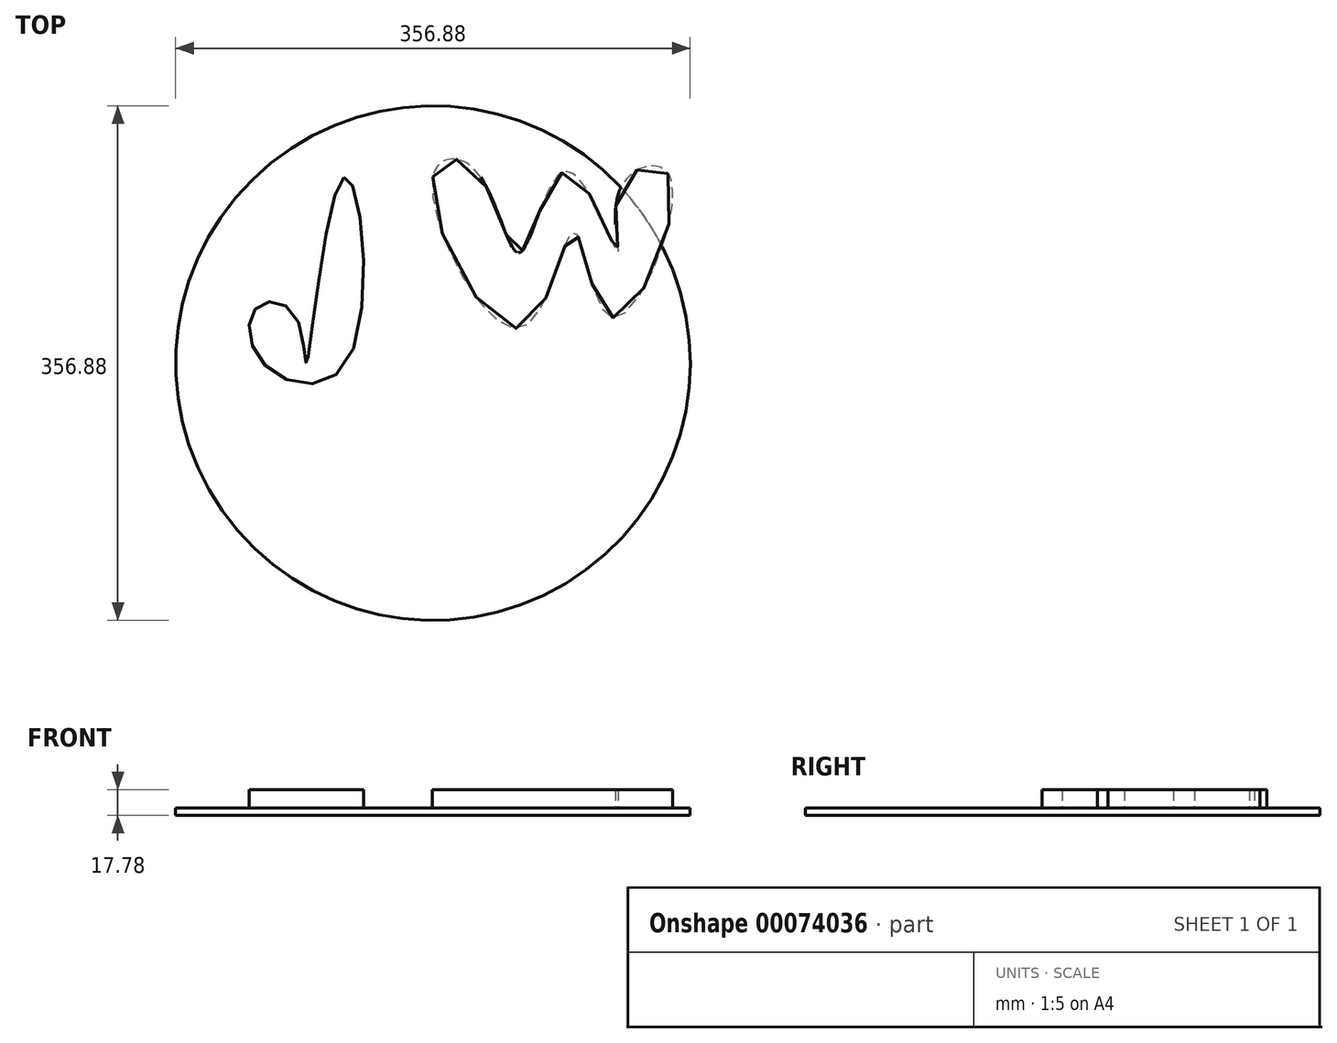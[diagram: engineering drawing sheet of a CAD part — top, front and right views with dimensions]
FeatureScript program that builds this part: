
annotation { "Feature Type Name" : "Feature", "Feature Type Description" : "" }
export const myFeature = defineFeature(function(context is Context, id is Id, definition is map)
    precondition{}
    {
        {
            var Q0;
            Q0=qCreatedBy(makeId("Top.planeOp"),FACE);
            var sketch = newSketch(context, id + "F0", { "sketchPlane" : qUnion([Q0])});
            skCircle(sketch, "E0", {"center": v(0, 0) * mm, "radius": 178.44 * mm});
            skSolve(sketch);
        }
        {
            var Q0;
            Q0=makeQuery(id+"F0.imprint","IMPRINT",FACE,{"disambiguationData":[TD([[makeQuery(id+"F0.imprint","IMPRINT",EDGE,{"derivedFrom":sQuery(id+"F0.wireOp",EDGE,"E0")}),1.0]])]});
            extrude(context, id + "F2", {"entities" : qUnion([Q0]), "depth" : 5.08 * mm});
        }
        {
            var Q0;
            Q0=makeQuery(id+"F2.opExtrude","CAP_FACE",FACE,{"disambiguationData":[OSD([sQuery(id+"F0.wireOp",EDGE,"E0")])],"isStart":false});
            var sketch = newSketch(context, id + "F3", { "sketchPlane" : qUnion([Q0])});
            skFitSpline(sketch, "E1", {"points": [v(-61.85, 129.01) * mm, v(-60.08, 0) * mm, v(-117.84, 0) * mm, v(-122.23, 38.62) * mm, v(-95.67, 33.35) * mm, v(-87.68, 0) * mm, v(-61.85, 129.01) * mm]});
            skFitSpline(sketch, "E2", {"points": [v(0, 129.21) * mm, v(61.34, 24.47) * mm, v(97.81, 91.15) * mm, v(124.24, 31.6) * mm, v(164.23, 129.21) * mm, v(130.34, 121.87) * mm, v(127.86, 76.84) * mm, v(92.38, 132.83) * mm, v(60.46, 76.84) * mm, v(28.52, 134.54) * mm, v(0, 129.21) * mm]});
            skSolve(sketch);
        }
        {
            var Q0;
            {var subQ0=sQuery(id+"F3.wireOp",EDGE,"E2");var subQ1=makeQuery(id+"F2.opExtrude","CAP_EDGE",EDGE,{"disambiguationData":[OSD([sQuery(id+"F0.wireOp",EDGE,"E0")])],"isStart":false});var subQ2=makeQuery(id+"F3.imprint","INTERSECT",VERTEX,{"disambiguationData":[OD(0.0)],"derivedFrom":[subQ1,subQ0]});Q0=makeQuery(id+"F3.imprint","IMPRINT",FACE,{"disambiguationData":[TD([[makeQuery(id+"F3.imprint","IMPRINT",EDGE,{"disambiguationData":[TD([[subQ2,-1.0]])],"derivedFrom":subQ0}),1.0]])]});}
            var Q1;
            {var subQ0=sQuery(id+"F3.wireOp",EDGE,"E2");var subQ1=makeQuery(id+"F2.opExtrude","CAP_EDGE",EDGE,{"disambiguationData":[OSD([sQuery(id+"F0.wireOp",EDGE,"E0")])],"isStart":false});var subQ2=makeQuery(id+"F3.imprint","INTERSECT",VERTEX,{"disambiguationData":[OD(0.0)],"derivedFrom":[subQ1,subQ0]});Q1=makeQuery(id+"F3.imprint","IMPRINT",FACE,{"disambiguationData":[TD([[makeQuery(id+"F3.imprint","IMPRINT",EDGE,{"disambiguationData":[TD([[subQ2,1.0]])],"derivedFrom":subQ0}),1.0]])]});}
            extrude(context, id + "F1", {"entities" : qUnion([Q0, Q1]), "operationType" : NewBodyOperationType.ADD, "depth" : 12.7 * mm});
        }
        {
            var Q0;
            Q0=makeQuery(id+"F3.imprint","IMPRINT",FACE,{"disambiguationData":[TD([[makeQuery(id+"F3.imprint","IMPRINT",EDGE,{"derivedFrom":sQuery(id+"F3.wireOp",EDGE,"E1")}),-1.0]])]});
            extrude(context, id + "F4", {"entities" : qUnion([Q0]), "operationType" : NewBodyOperationType.ADD, "depth" : 12.7 * mm});
        }
    });
